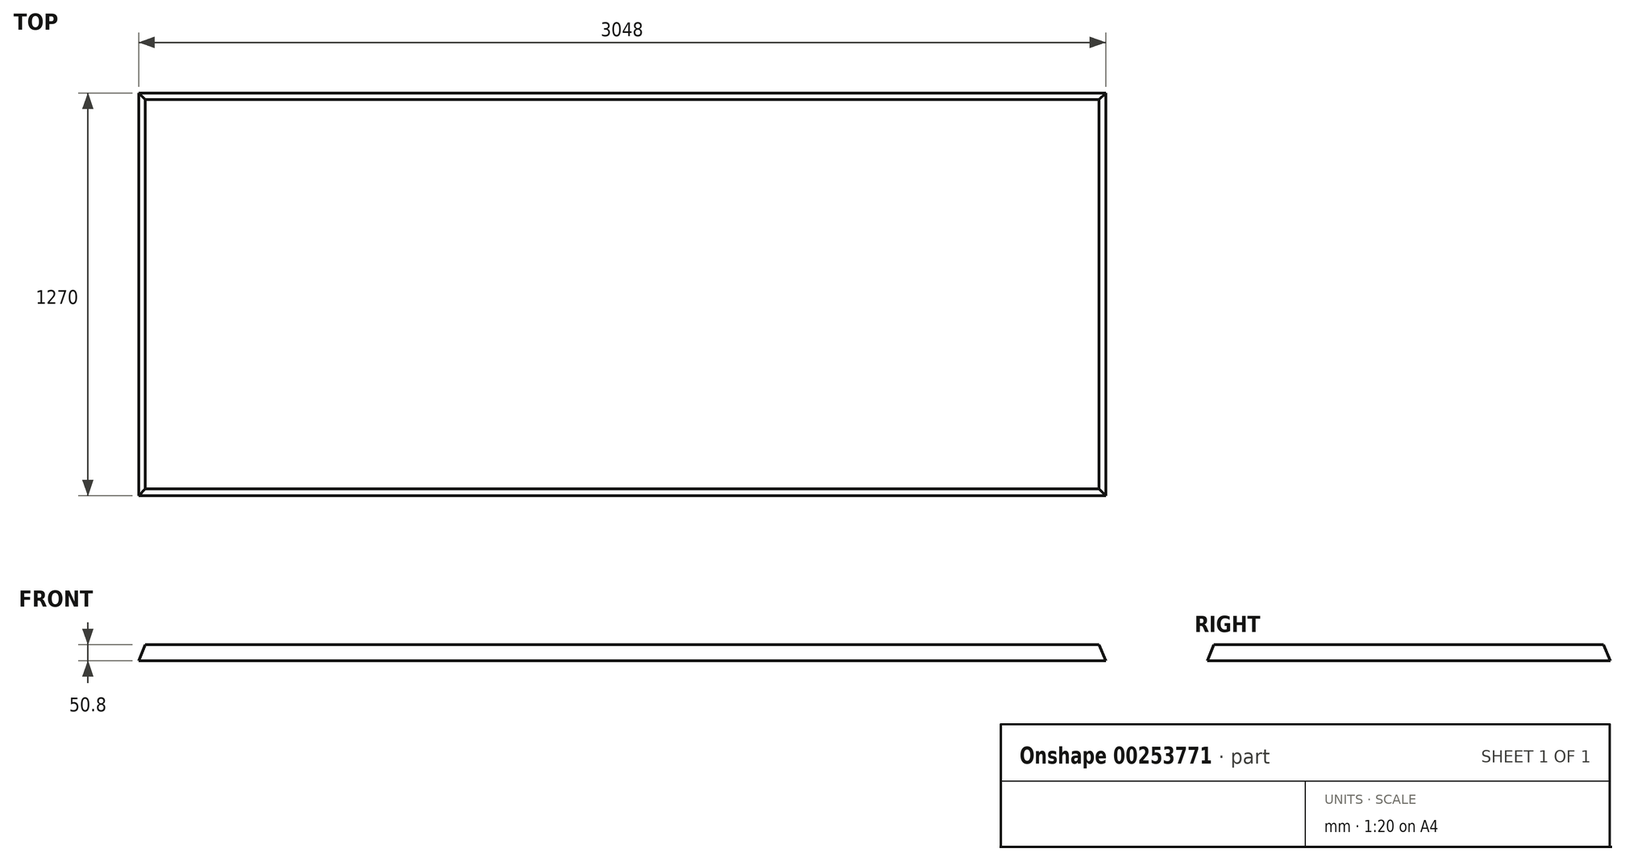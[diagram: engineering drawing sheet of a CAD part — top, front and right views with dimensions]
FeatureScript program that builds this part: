
annotation { "Feature Type Name" : "Feature", "Feature Type Description" : "" }
export const myFeature = defineFeature(function(context is Context, id is Id, definition is map)
    precondition{}
    {
        {
            var Q0;
            Q0=qCreatedBy(makeId("Top.planeOp"),FACE);
            var sketch = newSketch(context, id + "F0", { "sketchPlane" : qUnion([Q0])});
            skLineSegment(sketch, "E0.bottom", {"start": v(1524, -635) * mm, "end": v(-1524, -635) * mm});
            skLineSegment(sketch, "E0.top", {"start": v(1524, 635) * mm, "end": v(-1524, 635) * mm});
            skLineSegment(sketch, "E0.left", {"start": v(1524, -635) * mm, "end": v(1524, 635) * mm});
            skLineSegment(sketch, "E0.right", {"start": v(-1524, -635) * mm, "end": v(-1524, 635) * mm});
            skPoint(sketch, "E0.middle", {"position": v(0, 0) * mm});
            skSolve(sketch);
        }
        {
            var Q0;
            Q0=makeQuery(id+"F0.imprint","IMPRINT",FACE,{"disambiguationData":[TD([[makeQuery(id+"F0.imprint","IMPRINT",EDGE,{"derivedFrom":sQuery(id+"F0.wireOp",EDGE,"E0.bottom")}),-1.0]])]});
            extrude(context, id + "F1", {"entities" : qUnion([Q0]), "depth" : 50.8 * mm, "hasDraft" : true, "draftAngle" : 22.5 * degree, "draftPullDirection" : true});
        }
        {
            var Q0;
            Q0=makeQuery(id+"F1.opExtrude","CAP_FACE",FACE,{"disambiguationData":[OSD([sQuery(id+"F0.wireOp",EDGE,"E0.bottom"),sQuery(id+"F0.wireOp",EDGE,"E0.top"),sQuery(id+"F0.wireOp",EDGE,"E0.left"),sQuery(id+"F0.wireOp",EDGE,"E0.right")])],"isStart":false});
            var Q1;
            Q1=makeQuery(id+"F1.opExtrude","CAP_EDGE",EDGE,{"disambiguationData":[OSD([sQuery(id+"F0.wireOp",EDGE,"E0.top")])],"isStart":false});
            cPlane(context, id + "F2", {"entities" : qUnion([Q0, Q1]), "cplaneType" : CPlaneType.LINE_ANGLE, "offset" : 25.4 * mm, "angle" : 120 * degree, "width" : 152.4 * mm, "height" : 152.4 * mm});
        }
        {
            var Q0;
            Q0=makeQuery(id+"F1.opExtrude","CAP_FACE",FACE,{"disambiguationData":[OSD([sQuery(id+"F0.wireOp",EDGE,"E0.bottom"),sQuery(id+"F0.wireOp",EDGE,"E0.top"),sQuery(id+"F0.wireOp",EDGE,"E0.left"),sQuery(id+"F0.wireOp",EDGE,"E0.right")])],"isStart":true});
            var sketch = newSketch(context, id + "F3", { "sketchPlane" : qUnion([Q0])});
            skSolve(sketch);
        }
        {
            var Q0;
            Q0=makeQuery(id+"F1.opExtrude","CAP_VERTEX",VERTEX,{"disambiguationData":[OSD([sQuery(id+"F0.wireOp",EDGE,"E0.bottom"),sQuery(id+"F0.wireOp",EDGE,"E0.left")])],"isStart":true});
            var Q1;
            Q1=makeQuery(id+"F1.opExtrude","CAP_VERTEX",VERTEX,{"disambiguationData":[OSD([sQuery(id+"F0.wireOp",EDGE,"E0.bottom"),sQuery(id+"F0.wireOp",EDGE,"E0.left")])],"isStart":false});
            var Q2;
            Q2=makeQuery(id+"F1.opExtrude","CAP_VERTEX",VERTEX,{"disambiguationData":[OSD([sQuery(id+"F0.wireOp",EDGE,"E0.bottom"),sQuery(id+"F0.wireOp",EDGE,"E0.right")])],"isStart":false});
            cPlane(context, id + "F4", {"entities" : qUnion([Q0, Q1, Q2]), "cplaneType" : CPlaneType.THREE_POINT, "offset" : 25.4 * mm, "width" : 152.4 * mm, "height" : 152.4 * mm});
        }
    });
